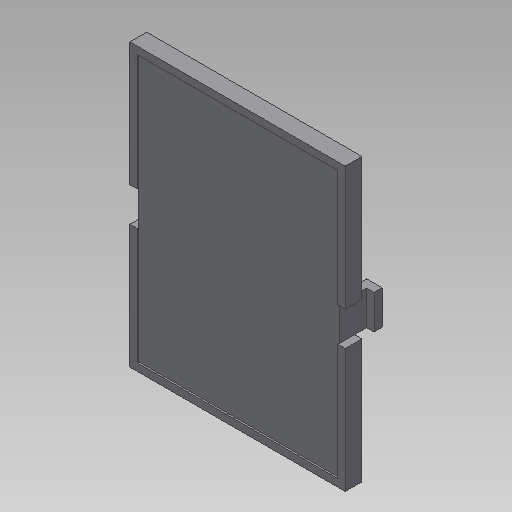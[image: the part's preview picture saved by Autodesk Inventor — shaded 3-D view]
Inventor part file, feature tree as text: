
AUTODESK INVENTOR PART (.ipt)
format: ipt  version: 2018 (Build 220112000, 112)  size: 158,720 bytes
history: native  units: mm
features: extrude x5, sketch x5, projected_geometry x3, other x1
ambient origin geometry x8: Origin, YZ Plane, XZ Plane, XY Plane, X Axis, Y Axis, Z Axis, Center Point
bodies: Body1 (feature_tree)
feature tree (14):
  other  "Твердое тело1"
  extrude  "Выдавливание1"  Depth=32.1mm
  extrude  "Выдавливание2"  Depth=42.0mm
  extrude  "Выдавливание3"  Depth=2.5mm TaperAngle=0.0deg
  extrude  "Выдавливание4"  Depth=2.3mm
  extrude  "Выдавливание5"  Depth=1.2mm
  sketch  "Эскиз1"
  sketch  "Эскиз2"
  projected_geometry  "Спроецированная петля1"
  sketch  "Эскиз3"
  projected_geometry  "Спроецированная петля2"
  projected_geometry  "Спроецированная петля3"
  sketch  "Эскиз4"
  sketch  "Эскиз5"
